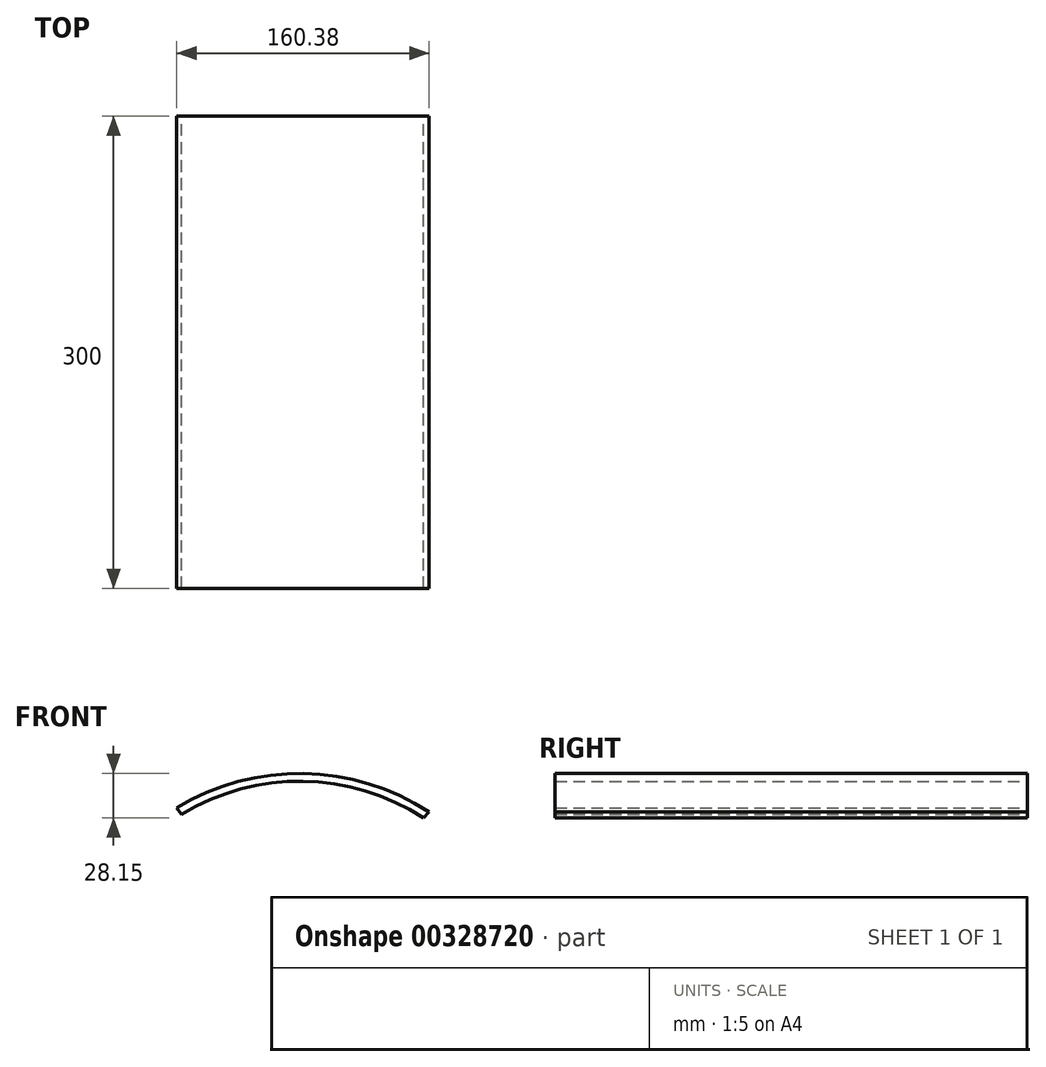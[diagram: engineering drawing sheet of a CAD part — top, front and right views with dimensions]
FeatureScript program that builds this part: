
annotation { "Feature Type Name" : "Feature", "Feature Type Description" : "" }
export const myFeature = defineFeature(function(context is Context, id is Id, definition is map)
    precondition{}
    {
        {
            var Q0;
            Q0=qCreatedBy(makeId("Front.planeOp"),FACE);
            var sketch = newSketch(context, id + "F0", { "sketchPlane" : qUnion([Q0])});
            skArc(sketch, "E0", {"start": v(82.27, 125.43) * mm, "mid": v(2.46, 149.98) * mm, "end": v(-78.11, 128.06) * mm});
            skArc(sketch, "E1", {"start": v(78.6, 121.85) * mm, "mid": v(2.12, 144.98) * mm, "end": v(-75, 124.1) * mm});
            skLineSegment(sketch, "E2", {"start": v(78.6, 121.85) * mm, "end": v(82.27, 125.43) * mm});
            skLineSegment(sketch, "E3", {"start": v(-75, 124.1) * mm, "end": v(-78.11, 128.06) * mm});
            skSolve(sketch);
        }
        {
            var Q0;
            Q0 = qSketchRegion(id + "F0", true);
            extrude(context, id + "F1", {"entities" : qUnion([Q0]), "depth" : 300 * mm});
        }
    });
